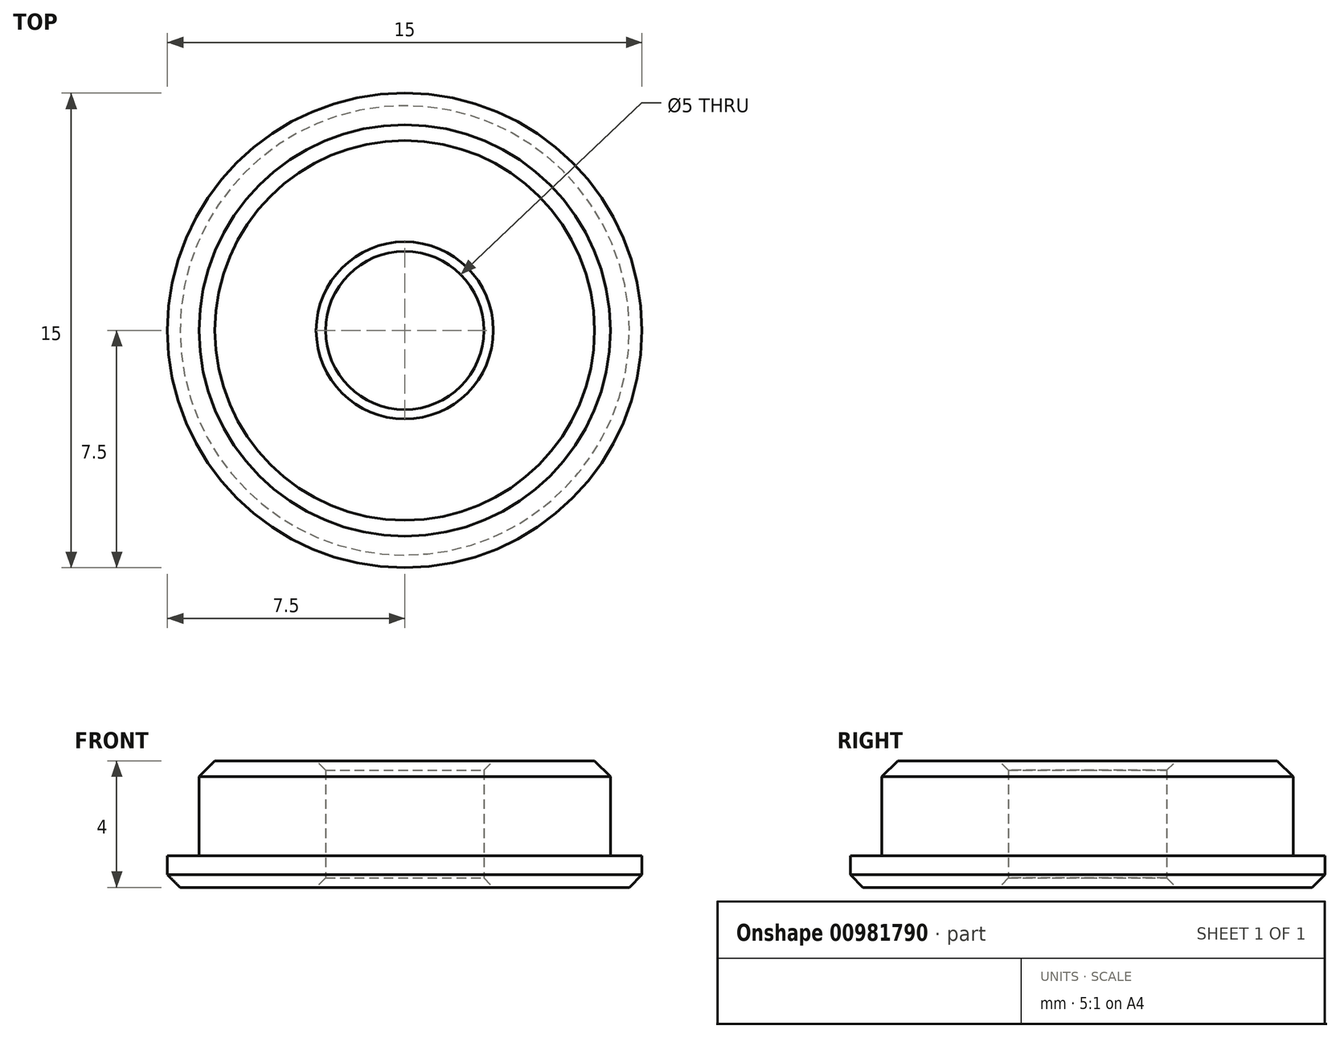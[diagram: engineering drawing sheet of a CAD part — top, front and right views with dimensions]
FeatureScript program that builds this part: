
annotation { "Feature Type Name" : "Feature", "Feature Type Description" : "" }
export const myFeature = defineFeature(function(context is Context, id is Id, definition is map)
    precondition{}
    {
        {
            var Q0;
            Q0=qCreatedBy(makeId("Front.planeOp"),FACE);
            var sketch = newSketch(context, id + "F0", { "sketchPlane" : qUnion([Q0])});
            skLineSegment(sketch, "E0", {"start": v(0, 0) * mm, "end": v(0, 20.88) * mm});
            skLineSegment(sketch, "E1", {"start": v(7.5, 0) * mm, "end": v(7.5, 1) * mm});
            skLineSegment(sketch, "E2", {"start": v(7.5, 1) * mm, "end": v(6.5, 1) * mm});
            skLineSegment(sketch, "E3", {"start": v(6.5, 1) * mm, "end": v(6.5, 4) * mm});
            skLineSegment(sketch, "E4", {"start": v(2.5, 4) * mm, "end": v(6.5, 4) * mm});
            skLineSegment(sketch, "E5", {"start": v(2.5, 4) * mm, "end": v(2.5, 0) * mm});
            skLineSegment(sketch, "E6", {"start": v(2.5, 0) * mm, "end": v(7.5, 0) * mm});
            skSolve(sketch);
        }
        {
            var Q0;
            Q0=qSketchRegion(id+"F0",true);
            var Q1;
            Q1=sQuery(id+"F0.wireOp",EDGE,"E0");
            revolve(context, id + "F1", {"surfaceOperationType" : NewSurfaceOperationType.NEW, "entities" : qUnion([Q0]), "axis" : qUnion([Q1]), "revolveType" : RevolveType.FULL});
        }
        {
            var Q0;
            Q0=makeQuery(id+"F1.opRevolve","SWEPT_EDGE",EDGE,{"disambiguationData":[OSD([sQuery(id+"F0.wireOp",EDGE,"E3"),sQuery(id+"F0.wireOp",EDGE,"E4")])]});
            chamfer(context, id + "F2", {"entities" : qUnion([Q0]), "width" : 0.5 * mm, "tangentPropagation" : true});
        }
        {
            var Q0;
            Q0=makeQuery(id+"F1.opRevolve","SWEPT_EDGE",EDGE,{"disambiguationData":[OSD([sQuery(id+"F0.wireOp",EDGE,"E1"),sQuery(id+"F0.wireOp",EDGE,"E6")])]});
            chamfer(context, id + "F3", {"entities" : qUnion([Q0]), "width" : 0.4 * mm, "tangentPropagation" : true});
        }
        {
            var Q0;
            Q0=makeQuery(id+"F1.opRevolve","SWEPT_EDGE",EDGE,{"disambiguationData":[OSD([sQuery(id+"F0.wireOp",EDGE,"E5"),sQuery(id+"F0.wireOp",EDGE,"E6")])]});
            var Q1;
            Q1=makeQuery(id+"F1.opRevolve","SWEPT_EDGE",EDGE,{"disambiguationData":[OSD([sQuery(id+"F0.wireOp",EDGE,"E4"),sQuery(id+"F0.wireOp",EDGE,"E5")])]});
            chamfer(context, id + "F4", {"entities" : qUnion([Q0, Q1]), "width" : 0.3 * mm, "tangentPropagation" : true});
        }
    });
